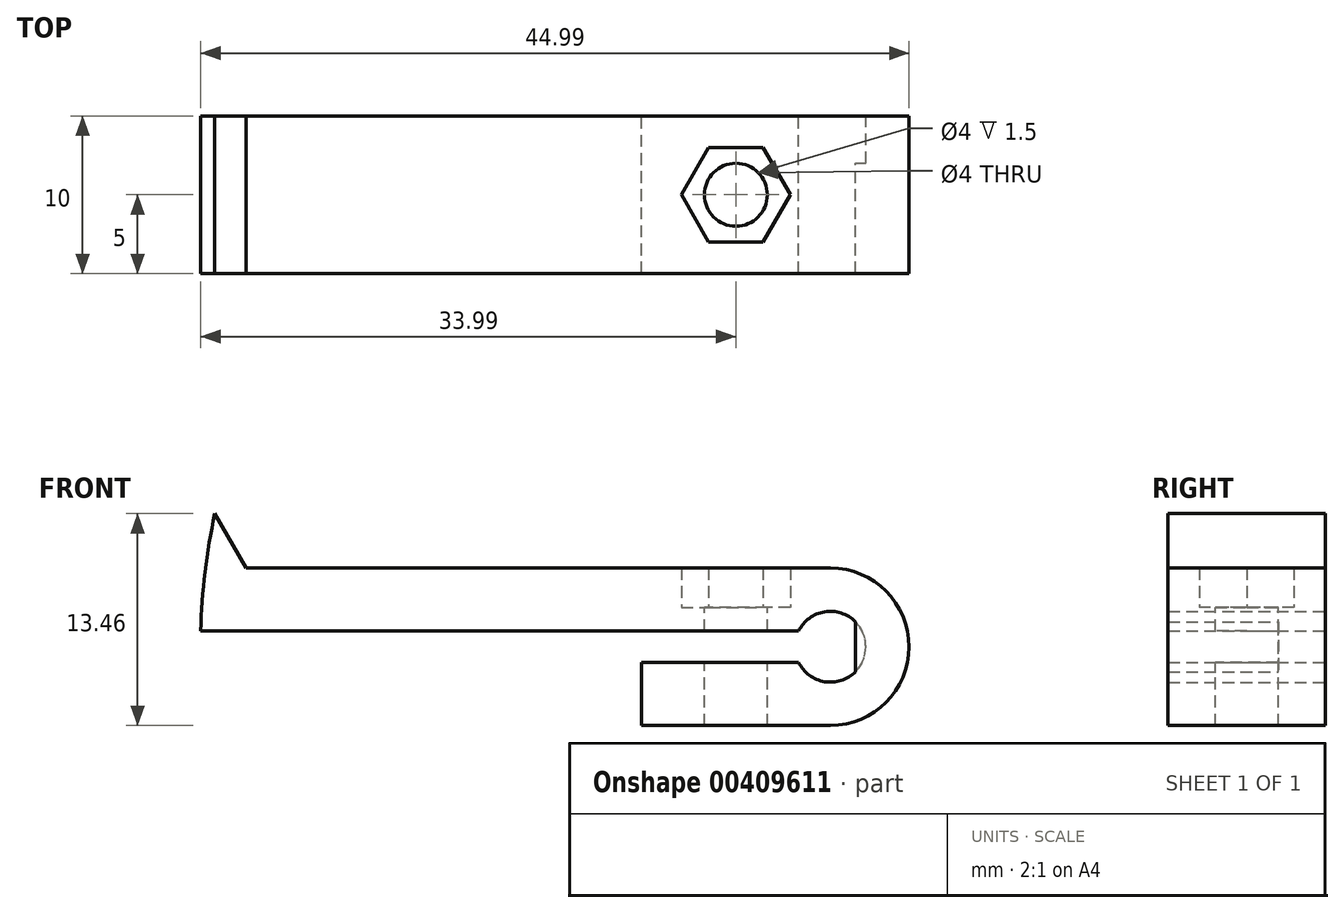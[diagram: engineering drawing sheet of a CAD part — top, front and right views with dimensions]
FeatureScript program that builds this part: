
annotation { "Feature Type Name" : "Feature", "Feature Type Description" : "" }
export const myFeature = defineFeature(function(context is Context, id is Id, definition is map)
    precondition{}
    {
        {
            var Q0;
            Q0=qCreatedBy(makeId("Front.planeOp"),FACE);
            var sketch = newSketch(context, id + "F0", { "sketchPlane" : qUnion([Q0])});
            skLineSegment(sketch, "E0", {"start": v(1.6, 1.6) * mm, "end": v(1.6, -1.6) * mm});
            skLineSegment(sketch, "E1", {"start": v(-37.1, 5) * mm, "end": v(-39.1, 8.46) * mm});
            skArc(sketch, "E2", {"start": v(-39.1, 8.46) * mm, "mid": v(-39.72, 4.75) * mm, "end": v(-39.99, 1) * mm});
            skArc(sketch, "E3", {"start": v(1.6, 1.6) * mm, "mid": v(-0.36, 2.22) * mm, "end": v(-2.02, 1) * mm});
            skArc(sketch, "E4", {"start": v(-2.02, -1) * mm, "mid": v(-0.36, -2.22) * mm, "end": v(1.6, -1.6) * mm});
            skArc(sketch, "E5", {"start": v(0, 5) * mm, "mid": v(5, 0) * mm, "end": v(0, -5) * mm});
            skCircle(sketch, "E6", {"center": v(0, 0) * mm, "radius": 2.25 * mm, "construction": true});
            skPoint(sketch, "E7", {"position": v(-2.25, 0) * mm});
            skCircle(sketch, "E8", {"center": v(0, 0) * mm, "radius": 5 * mm, "construction": true});
            skLineSegment(sketch, "E9", {"start": v(-37.1, 5) * mm, "end": v(0, 5) * mm});
            skLineSegment(sketch, "E10", {"start": v(0, -5) * mm, "end": v(-12, -5) * mm});
            skLineSegment(sketch, "E11", {"start": v(-12, -5) * mm, "end": v(-12, -1) * mm});
            skLineSegment(sketch, "E12", {"start": v(-2.02, -1) * mm, "end": v(-12, -1) * mm});
            skLineSegment(sketch, "E13", {"start": v(-2.02, 1) * mm, "end": v(-39.99, 1) * mm});
            skLineSegment(sketch, "E14", {"start": v(0, 0) * mm, "end": v(1.6, 1.6) * mm, "construction": true});
            skLineSegment(sketch, "E15", {"start": v(0, 0) * mm, "end": v(1.6, -1.6) * mm, "construction": true});
            skSolve(sketch);
        }
        {
            var Q0;
            Q0=qCreatedBy(makeId("Top.planeOp"),FACE);
            var sketch = newSketch(context, id + "F1", { "sketchPlane" : qUnion([Q0])});
            skCircle(sketch, "E16", {"center": v(-6, 0) * mm, "radius": 2 * mm});
            skSolve(sketch);
        }
        {
            var Q0;
            Q0=qCreatedBy(makeId("Top.planeOp"),FACE);
            var sketch = newSketch(context, id + "F2", { "sketchPlane" : qUnion([Q0])});
            skCircle(sketch, "E17.cCircle", {"center": v(-6, 0) * mm, "radius": 3 * mm, "construction": true});
            skLineSegment(sketch, "E17.0", {"start": v(-2.54, 0) * mm, "end": v(-4.27, -3) * mm});
            skLineSegment(sketch, "E17.1", {"start": v(-4.27, -3) * mm, "end": v(-7.73, -3) * mm});
            skLineSegment(sketch, "E17.2", {"start": v(-7.73, -3) * mm, "end": v(-9.46, 0) * mm});
            skLineSegment(sketch, "E17.3", {"start": v(-9.46, 0) * mm, "end": v(-7.73, 3) * mm});
            skLineSegment(sketch, "E17.4", {"start": v(-7.73, 3) * mm, "end": v(-4.27, 3) * mm});
            skLineSegment(sketch, "E17.5", {"start": v(-4.27, 3) * mm, "end": v(-2.54, 0) * mm});
            skPoint(sketch, "E17.0.midPoint", {"position": v(-3.4, -1.5) * mm});
            skSolve(sketch);
        }
        {
            var Q0;
            Q0=qCreatedBy(makeId("Front.planeOp"),FACE);
            var sketch = newSketch(context, id + "F3", { "sketchPlane" : qUnion([Q0])});
            skCircle(sketch, "E18", {"center": v(0, 0) * mm, "radius": 2.25 * mm});
            skSolve(sketch);
        }
        {
            var Q0;
            Q0 = qSketchRegion(id + "F0", true);
            extrude(context, id + "F4", {"entities" : qUnion([Q0]), "depth" : 5 * mm, "hasSecondDirection" : true, "secondDirectionOppositeDirection" : true, "secondDirectionDepth" : 5 * mm});
        }
        {
            var Q0;
            Q0 = qSketchRegion(id + "F1", true);
            extrude(context, id + "F5", {"entities" : qUnion([Q0]), "operationType" : NewBodyOperationType.REMOVE, "oppositeDirection" : true, "depth" : 12 * mm, "hasSecondDirection" : true, "secondDirectionOppositeDirection" : false, "secondDirectionDepth" : 25 * mm});
        }
        {
            var Q0;
            Q0 = qSketchRegion(id + "F2", true);
            extrude(context, id + "F6", {"entities" : qUnion([Q0]), "operationType" : NewBodyOperationType.REMOVE, "depth" : 6 * mm, "hasSecondDirection" : true, "secondDirectionOppositeDirection" : false, "secondDirectionDepth" : 2.5 * mm});
        }
        {
            var Q0;
            Q0 = qSketchRegion(id + "F3", true);
            extrude(context, id + "F7", {"entities" : qUnion([Q0]), "operationType" : NewBodyOperationType.REMOVE, "oppositeDirection" : true, "depth" : 25 * mm, "hasSecondDirection" : true, "secondDirectionOppositeDirection" : true, "secondDirectionDepth" : 2 * mm});
        }
    });
